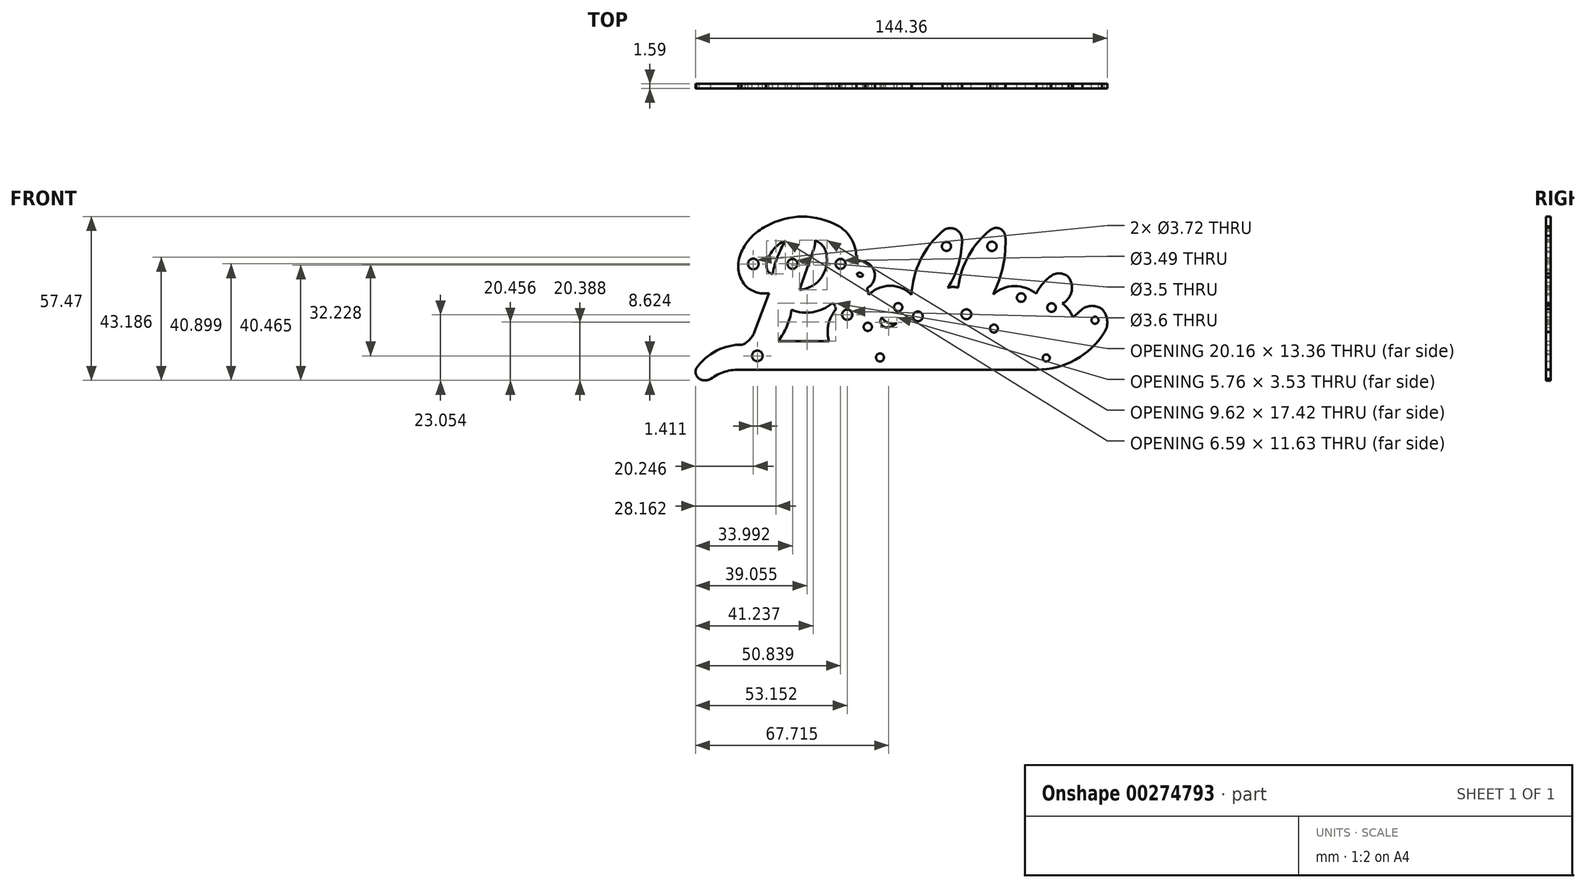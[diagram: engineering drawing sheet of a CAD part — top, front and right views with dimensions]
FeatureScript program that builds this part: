
annotation { "Feature Type Name" : "Feature", "Feature Type Description" : "" }
export const myFeature = defineFeature(function(context is Context, id is Id, definition is map)
    precondition{}
    {
        {
            var Q0;
            Q0=qCreatedBy(makeId("Front.planeOp"),FACE);
            var sketch = newSketch(context, id + "F0", { "sketchPlane" : qUnion([Q0])});
            skArc(sketch, "E0", {"start": v(-57.9, -15.93) * mm, "mid": v(-67.04, -18.07) * mm, "end": v(-74.11, -24.24) * mm});
            skArc(sketch, "E1", {"start": v(-74.11, -24.24) * mm, "mid": v(-74.29, -26.27) * mm, "end": v(-73.08, -27.9) * mm});
            skArc(sketch, "E2", {"start": v(-73.08, -27.9) * mm, "mid": v(-71.07, -28.5) * mm, "end": v(-69.07, -27.9) * mm});
            skArc(sketch, "E3", {"start": v(-58.44, -24.74) * mm, "mid": v(-64.03, -25.4) * mm, "end": v(-69.07, -27.9) * mm});
            skLineSegment(sketch, "E4", {"start": v(-58.44, -24.74) * mm, "end": v(45.18, -24.74) * mm});
            skArc(sketch, "E5", {"start": v(45.18, -24.74) * mm, "mid": v(58.78, -21.23) * mm, "end": v(68.99, -11.6) * mm});
            skArc(sketch, "E6", {"start": v(68.99, -11.6) * mm, "mid": v(69.92, -7.35) * mm, "end": v(68.05, -3.43) * mm});
            skArc(sketch, "E7", {"start": v(68.05, -3.43) * mm, "mid": v(64.63, -2.34) * mm, "end": v(61.22, -3.43) * mm});
            skArc(sketch, "E8", {"start": v(57.89, -6.37) * mm, "mid": v(59.57, -4.92) * mm, "end": v(61.22, -3.43) * mm});
            skArc(sketch, "E9", {"start": v(57.89, -6.37) * mm, "mid": v(56.42, -3.68) * mm, "end": v(54.26, -1.49) * mm});
            skArc(sketch, "E10", {"start": v(54.26, -1.49) * mm, "mid": v(57.42, 2.6) * mm, "end": v(56.42, 7.68) * mm});
            skArc(sketch, "E11", {"start": v(56.42, 7.68) * mm, "mid": v(53.43, 9.08) * mm, "end": v(50.25, 8.16) * mm});
            skArc(sketch, "E12", {"start": v(50.25, 8.16) * mm, "mid": v(47.25, 5.36) * mm, "end": v(45.05, 1.9) * mm});
            skArc(sketch, "E13", {"start": v(45.05, 1.9) * mm, "mid": v(37.45, 4.6) * mm, "end": v(29.94, 1.68) * mm});
            skArc(sketch, "E14", {"start": v(29.94, 1.68) * mm, "mid": v(33.45, 11.66) * mm, "end": v(34.2, 22.22) * mm});
            skArc(sketch, "E15", {"start": v(34.2, 22.22) * mm, "mid": v(32.22, 24.77) * mm, "end": v(29.02, 24.33) * mm});
            skArc(sketch, "E16", {"start": v(29.02, 24.33) * mm, "mid": v(21.36, 15.3) * mm, "end": v(17.69, 4.06) * mm});
            skArc(sketch, "E17", {"start": v(17.69, 4.06) * mm, "mid": v(15.87, 4.29) * mm, "end": v(14.04, 4.06) * mm});
            skArc(sketch, "E18", {"start": v(14.04, 4.06) * mm, "mid": v(17.78, 12.22) * mm, "end": v(19.02, 21.1) * mm});
            skArc(sketch, "E19", {"start": v(19.02, 21.1) * mm, "mid": v(16.48, 24.64) * mm, "end": v(12.2, 23.88) * mm});
            skArc(sketch, "E20", {"start": v(12.2, 23.88) * mm, "mid": v(4.5, 13.8) * mm, "end": v(1.33, 1.51) * mm});
            skArc(sketch, "E21", {"start": v(1.33, 1.51) * mm, "mid": v(-6.17, 4.7) * mm, "end": v(-13.66, 1.51) * mm});
            skArc(sketch, "E22", {"start": v(-14.24, 3.9) * mm, "mid": v(-13.97, 2.7) * mm, "end": v(-13.66, 1.51) * mm});
            skArc(sketch, "E23", {"start": v(-14.24, 3.9) * mm, "mid": v(-11.55, 8.68) * mm, "end": v(-14.82, 13.07) * mm});
            skArc(sketch, "E24", {"start": v(-14.82, 13.07) * mm, "mid": v(-16.5, 13.41) * mm, "end": v(-18.2, 13.07) * mm});
            skArc(sketch, "E25", {"start": v(-18.2, 13.07) * mm, "mid": v(-19.25, 20.17) * mm, "end": v(-24.03, 25.53) * mm});
            skArc(sketch, "E26", {"start": v(-24.03, 25.53) * mm, "mid": v(-36.9, 28.97) * mm, "end": v(-49.78, 25.53) * mm});
            skArc(sketch, "E27", {"start": v(-49.78, 25.53) * mm, "mid": v(-54.87, 21.75) * mm, "end": v(-58.4, 16.48) * mm});
            skArc(sketch, "E28", {"start": v(-58.4, 16.48) * mm, "mid": v(-59.39, 10.48) * mm, "end": v(-57.07, 4.85) * mm});
            skArc(sketch, "E29", {"start": v(-57.07, 4.85) * mm, "mid": v(-53.22, 2.45) * mm, "end": v(-48.69, 2.16) * mm});
            skLineSegment(sketch, "E30", {"start": v(-48.69, 2.16) * mm, "end": v(-53.67, -11.34) * mm});
            skArc(sketch, "E31", {"start": v(-57.9, -15.93) * mm, "mid": v(-55.33, -14.05) * mm, "end": v(-53.67, -11.34) * mm});
            skArc(sketch, "E32", {"start": v(-42.94, 20.5) * mm, "mid": v(-47.25, 17.28) * mm, "end": v(-49.49, 12.4) * mm});
            skArc(sketch, "E33", {"start": v(-42.94, 20.5) * mm, "mid": v(-45.66, 14.87) * mm, "end": v(-47.42, 8.87) * mm});
            skArc(sketch, "E34", {"start": v(-49.49, 12.4) * mm, "mid": v(-49.5, 11.18) * mm, "end": v(-49.15, 10) * mm});
            skArc(sketch, "E35", {"start": v(-49.15, 10) * mm, "mid": v(-48.42, 9.23) * mm, "end": v(-47.42, 8.87) * mm});
            skArc(sketch, "E36", {"start": v(-28.37, 14.57) * mm, "mid": v(-29.49, 18.28) * mm, "end": v(-32.52, 20.68) * mm});
            skArc(sketch, "E37", {"start": v(-31.58, 6) * mm, "mid": v(-29.04, 9.93) * mm, "end": v(-28.37, 14.57) * mm});
            skArc(sketch, "E38", {"start": v(-37.97, 3.26) * mm, "mid": v(-34.57, 4.14) * mm, "end": v(-31.58, 6) * mm});
            skArc(sketch, "E39", {"start": v(-32.81, 18.14) * mm, "mid": v(-32.51, 19.4) * mm, "end": v(-32.52, 20.68) * mm});
            skLineSegment(sketch, "E40", {"start": v(-37.97, 3.26) * mm, "end": v(-32.81, 18.14) * mm});
            skArc(sketch, "E41", {"start": v(-45.42, -14.73) * mm, "mid": v(-42.38, -9.52) * mm, "end": v(-40.76, -3.7) * mm});
            skArc(sketch, "E42", {"start": v(-40.76, -3.7) * mm, "mid": v(-33.29, -4.54) * mm, "end": v(-26.47, -1.36) * mm});
            skArc(sketch, "E43", {"start": v(-25.27, -3.7) * mm, "mid": v(-25.53, -2.36) * mm, "end": v(-26.47, -1.36) * mm});
            skArc(sketch, "E44", {"start": v(-25.27, -3.7) * mm, "mid": v(-27.32, -7.15) * mm, "end": v(-28.07, -11.08) * mm});
            skArc(sketch, "E45", {"start": v(-28.07, -11.08) * mm, "mid": v(-28.01, -12.93) * mm, "end": v(-27.56, -14.73) * mm});
            skLineSegment(sketch, "E46", {"start": v(-45.42, -14.73) * mm, "end": v(-27.56, -14.73) * mm});
            skArc(sketch, "E47", {"start": v(-9.07, -6.35) * mm, "mid": v(-6.8, -8.32) * mm, "end": v(-3.8, -8.33) * mm});
            skArc(sketch, "E48", {"start": v(-9.07, -6.35) * mm, "mid": v(-9.43, -8.51) * mm, "end": v(-7.7, -9.88) * mm});
            skArc(sketch, "E49", {"start": v(-7.7, -9.88) * mm, "mid": v(-5.6, -9.5) * mm, "end": v(-3.8, -8.33) * mm});
            skArc(sketch, "E50", {"start": v(-47.16, 4.7) * mm, "mid": v(-46.47, 5.52) * mm, "end": v(-47.03, 6.44) * mm});
            skCircle(sketch, "E51", {"center": v(-52.74, -19.88) * mm, "radius": 1.86 * mm});
            skCircle(sketch, "E52", {"center": v(-54.15, 12.35) * mm, "radius": 1.86 * mm});
            skCircle(sketch, "E53", {"center": v(48.57, -20.61) * mm, "radius": 1.23 * mm});
            skCircle(sketch, "E54", {"center": v(50.42, -2.93) * mm, "radius": 1.5 * mm});
            skArc(sketch, "E55", {"start": v(-15.7, 8.3) * mm, "mid": v(-16.56, 9.2) * mm, "end": v(-17.77, 8.91) * mm});
            skArc(sketch, "E56", {"start": v(-17.77, 8.91) * mm, "mid": v(-16.95, 7.88) * mm, "end": v(-15.7, 8.3) * mm});
            skCircle(sketch, "E57", {"center": v(-23.56, 12.4) * mm, "radius": 1.74 * mm});
            skCircle(sketch, "E58", {"center": v(-40.4, 12.4) * mm, "radius": 1.75 * mm});
            skCircle(sketch, "E59", {"center": v(-21.25, -5.45) * mm, "radius": 1.8 * mm});
            skCircle(sketch, "E60", {"center": v(-3.36, -2.8) * mm, "radius": 1.44 * mm});
            skCircle(sketch, "E61", {"center": v(3.55, -6.04) * mm, "radius": 1.71 * mm});
            skCircle(sketch, "E62", {"center": v(13.55, 18.53) * mm, "radius": 1.6 * mm});
            skCircle(sketch, "E63", {"center": v(29.52, 18.53) * mm, "radius": 1.64 * mm});
            skCircle(sketch, "E64", {"center": v(20.54, -5.3) * mm, "radius": 1.74 * mm});
            skCircle(sketch, "E65", {"center": v(39.77, 0.56) * mm, "radius": 1.5 * mm});
            skCircle(sketch, "E66", {"center": v(-9.74, -20.45) * mm, "radius": 1.42 * mm});
            skCircle(sketch, "E67", {"center": v(-14.02, -9.7) * mm, "radius": 1.44 * mm});
            skCircle(sketch, "E68", {"center": v(30.2, -10.3) * mm, "radius": 1.39 * mm});
            skCircle(sketch, "E69", {"center": v(65.66, -7.36) * mm, "radius": 1.23 * mm});
            skSolve(sketch);
        }
        {
            var Q0;
            Q0=makeQuery(id+"F0.imprint","IMPRINT",FACE,{"disambiguationData":[TD([[makeQuery(id+"F0.imprint","IMPRINT",EDGE,{"derivedFrom":sQuery(id+"F0.wireOp",EDGE,"E0")}),1.0]])]});
            extrude(context, id + "F1", {"entities" : qUnion([Q0]), "depth" : 1.59 * mm});
        }
    });
